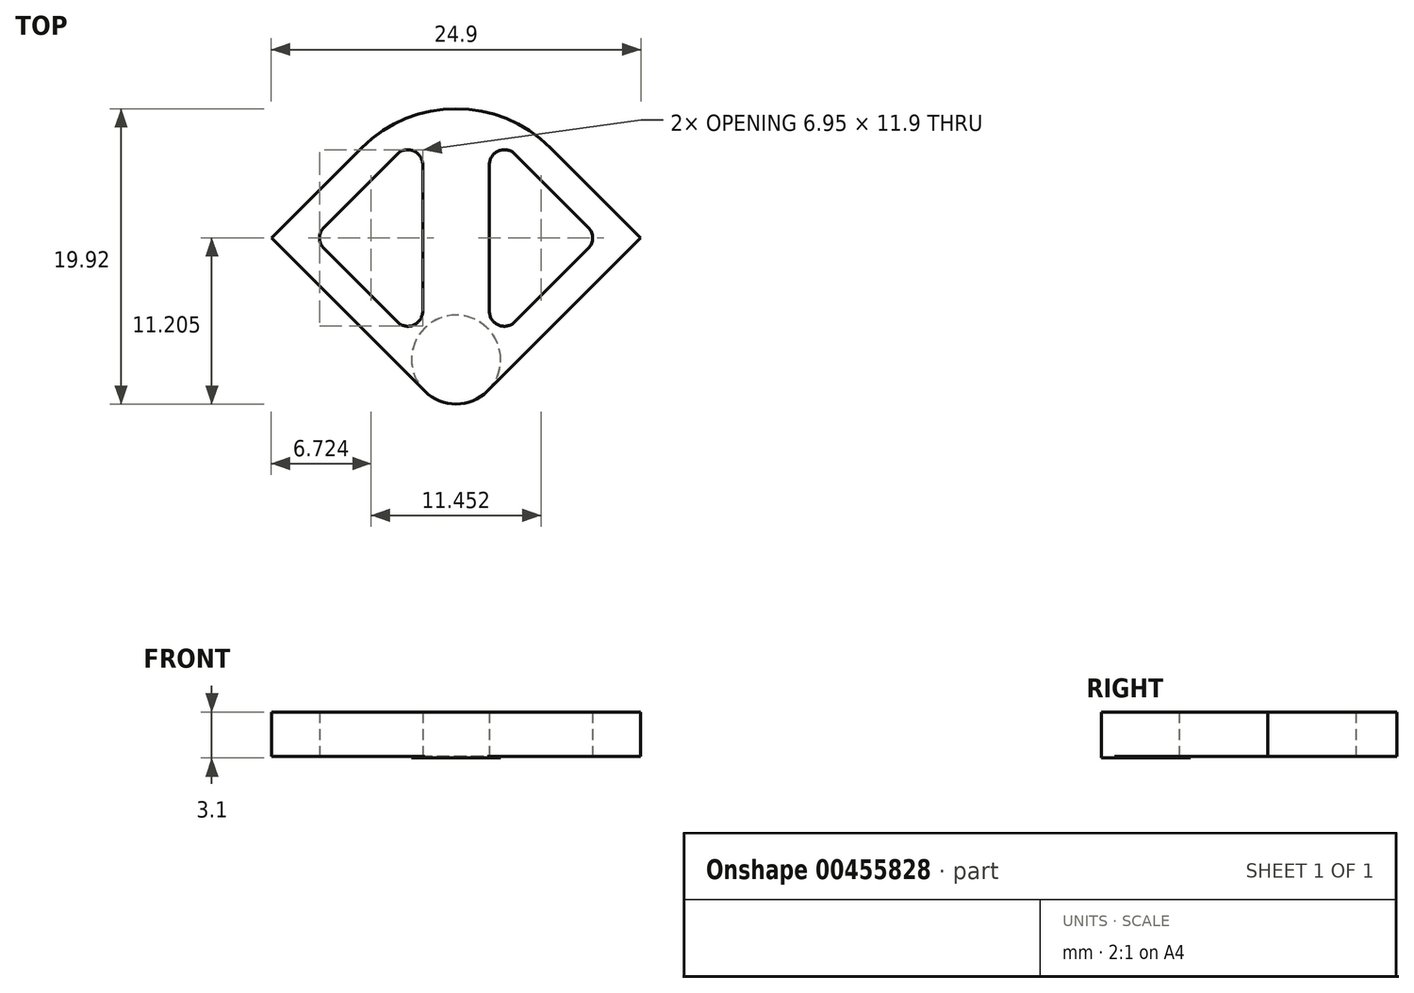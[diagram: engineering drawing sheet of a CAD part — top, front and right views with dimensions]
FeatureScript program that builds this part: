
annotation { "Feature Type Name" : "Feature", "Feature Type Description" : "" }
export const myFeature = defineFeature(function(context is Context, id is Id, definition is map)
    precondition{}
    {
        {
            var Q0;
            Q0=qCreatedBy(makeId("Top.planeOp"),FACE);
            var sketch = newSketch(context, id + "F0", { "sketchPlane" : qUnion([Q0])});
            skLineSegment(sketch, "E0", {"start": v(-2.12, 2.12) * mm, "end": v(-12.45, 12.45) * mm});
            skLineSegment(sketch, "E1", {"start": v(2.12, 2.12) * mm, "end": v(12.45, 12.45) * mm});
            skLineSegment(sketch, "E2", {"start": v(-12.45, 12.45) * mm, "end": v(-6.36, 18.53) * mm});
            skLineSegment(sketch, "E3", {"start": v(6.36, 18.53) * mm, "end": v(12.45, 12.45) * mm});
            skLineSegment(sketch, "E4", {"start": v(-8.9, 13.15) * mm, "end": v(-3.96, 18.1) * mm});
            skLineSegment(sketch, "E5", {"start": v(2.25, 17.4) * mm, "end": v(2.25, 7.5) * mm});
            skLineSegment(sketch, "E6", {"start": v(-2.25, 17.4) * mm, "end": v(-2.25, 7.5) * mm});
            skPoint(sketch, "E7.visualSharp", {"position": v(0, 0) * mm});
            skArc(sketch, "E7.filletArc", {"start": v(-2.12, 2.12) * mm, "mid": v(0, 1.24) * mm, "end": v(2.12, 2.12) * mm});
            skLineSegment(sketch, "E8", {"start": v(3.25, 3.25) * mm, "end": v(3.25, -3.76) * mm});
            skLineSegment(sketch, "E9", {"start": v(3.25, -3.76) * mm, "end": v(1.25, -3.76) * mm});
            skLineSegment(sketch, "E10", {"start": v(-3.25, -3.76) * mm, "end": v(-3.25, 3.25) * mm});
            skLineSegment(sketch, "E11", {"start": v(-8.9, 11.74) * mm, "end": v(-3.96, 6.79) * mm});
            skLineSegment(sketch, "E12", {"start": v(8.9, 11.74) * mm, "end": v(3.96, 6.79) * mm});
            skArc(sketch, "E13.filletArc", {"start": v(-8.9, 13.15) * mm, "mid": v(-9.2, 12.45) * mm, "end": v(-8.9, 11.74) * mm});
            skPoint(sketch, "E14.newPointA", {"position": v(11.03, 11.03) * mm});
            skArc(sketch, "E15.filletArc", {"start": v(2.25, 7.5) * mm, "mid": v(2.87, 6.57) * mm, "end": v(3.96, 6.79) * mm});
            skArc(sketch, "E16.filletArc", {"start": v(-3.96, 6.79) * mm, "mid": v(-2.87, 6.57) * mm, "end": v(-2.25, 7.5) * mm});
            skPoint(sketch, "E17.visualSharp", {"position": v(0, 24.9) * mm});
            skArc(sketch, "E18.filletArc", {"start": v(-2.25, 17.4) * mm, "mid": v(-2.87, 18.32) * mm, "end": v(-3.96, 18.1) * mm});
            skArc(sketch, "E19.filletArc", {"start": v(6.36, 18.53) * mm, "mid": v(0, 21.16) * mm, "end": v(-6.36, 18.53) * mm});
            skLineSegment(sketch, "E20", {"start": v(12.45, 12.45) * mm, "end": v(15, 9.89) * mm});
            skLineSegment(sketch, "E21", {"start": v(-12.45, 12.45) * mm, "end": v(-15.3, 9.59) * mm});
            skArc(sketch, "E22", {"start": v(1.25, -1.76) * mm, "mid": v(0, -0.5) * mm, "end": v(-1.25, -1.76) * mm});
            skLineSegment(sketch, "E23", {"start": v(-1.25, -1.76) * mm, "end": v(-1.25, -3.76) * mm});
            skLineSegment(sketch, "E24", {"start": v(1.25, -3.76) * mm, "end": v(1.25, -1.76) * mm});
            skLineSegment(sketch, "E25.trimOffspring", {"start": v(-1.25, -3.76) * mm, "end": v(-3.25, -3.76) * mm});
            skLineSegment(sketch, "E26", {"start": v(3.96, 18.1) * mm, "end": v(8.9, 13.15) * mm});
            skArc(sketch, "E27.filletArc", {"start": v(8.9, 11.74) * mm, "mid": v(9.2, 12.45) * mm, "end": v(8.9, 13.15) * mm});
            skArc(sketch, "E28.filletArc", {"start": v(3.96, 18.1) * mm, "mid": v(2.87, 18.32) * mm, "end": v(2.25, 17.4) * mm});
            skCircle(sketch, "E29", {"center": v(0, 4.24) * mm, "radius": 3 * mm});
            skSolve(sketch);
        }
        {
            var Q0;
            {var subQ2=sQuery(id+"F0.wireOp",EDGE,"E2");Q0=makeQuery(id+"F0.imprint","IMPRINT",FACE,{"disambiguationData":[TD([[makeQuery(id+"F0.imprint","IMPRINT",EDGE,{"derivedFrom":subQ2}),-1.0]])]});}
            var Q1;
            {var subQ0=sQuery(id+"F0.wireOp",EDGE,"E29");var subQ1=makeQuery(id+"F0.imprint","INTERSECT",VERTEX,{"derivedFrom":[sQuery(id+"F0.wireOp",EDGE,"E0"),subQ0]});Q1=makeQuery(id+"F0.imprint","IMPRINT",FACE,{"disambiguationData":[TD([[makeQuery(id+"F0.imprint","IMPRINT",EDGE,{"disambiguationData":[TD([[subQ1,-1.0]])],"derivedFrom":subQ0}),1.0]])]});}
            extrude(context, id + "F1", {"entities" : qUnion([Q0, Q1]), "depth" : 3 * mm});
        }
        {
            var Q0;
            {var subQ0=sQuery(id+"F0.wireOp",EDGE,"E29");var subQ1=makeQuery(id+"F0.imprint","INTERSECT",VERTEX,{"derivedFrom":[sQuery(id+"F0.wireOp",EDGE,"E0"),subQ0]});Q0=makeQuery(id+"F0.imprint","IMPRINT",FACE,{"disambiguationData":[TD([[makeQuery(id+"F0.imprint","IMPRINT",EDGE,{"disambiguationData":[TD([[subQ1,-1.0]])],"derivedFrom":subQ0}),1.0]])]});}
            extrude(context, id + "F2", {"entities" : qUnion([Q0]), "operationType" : NewBodyOperationType.ADD, "oppositeDirection" : true, "depth" : 0.1 * mm});
        }
    });
